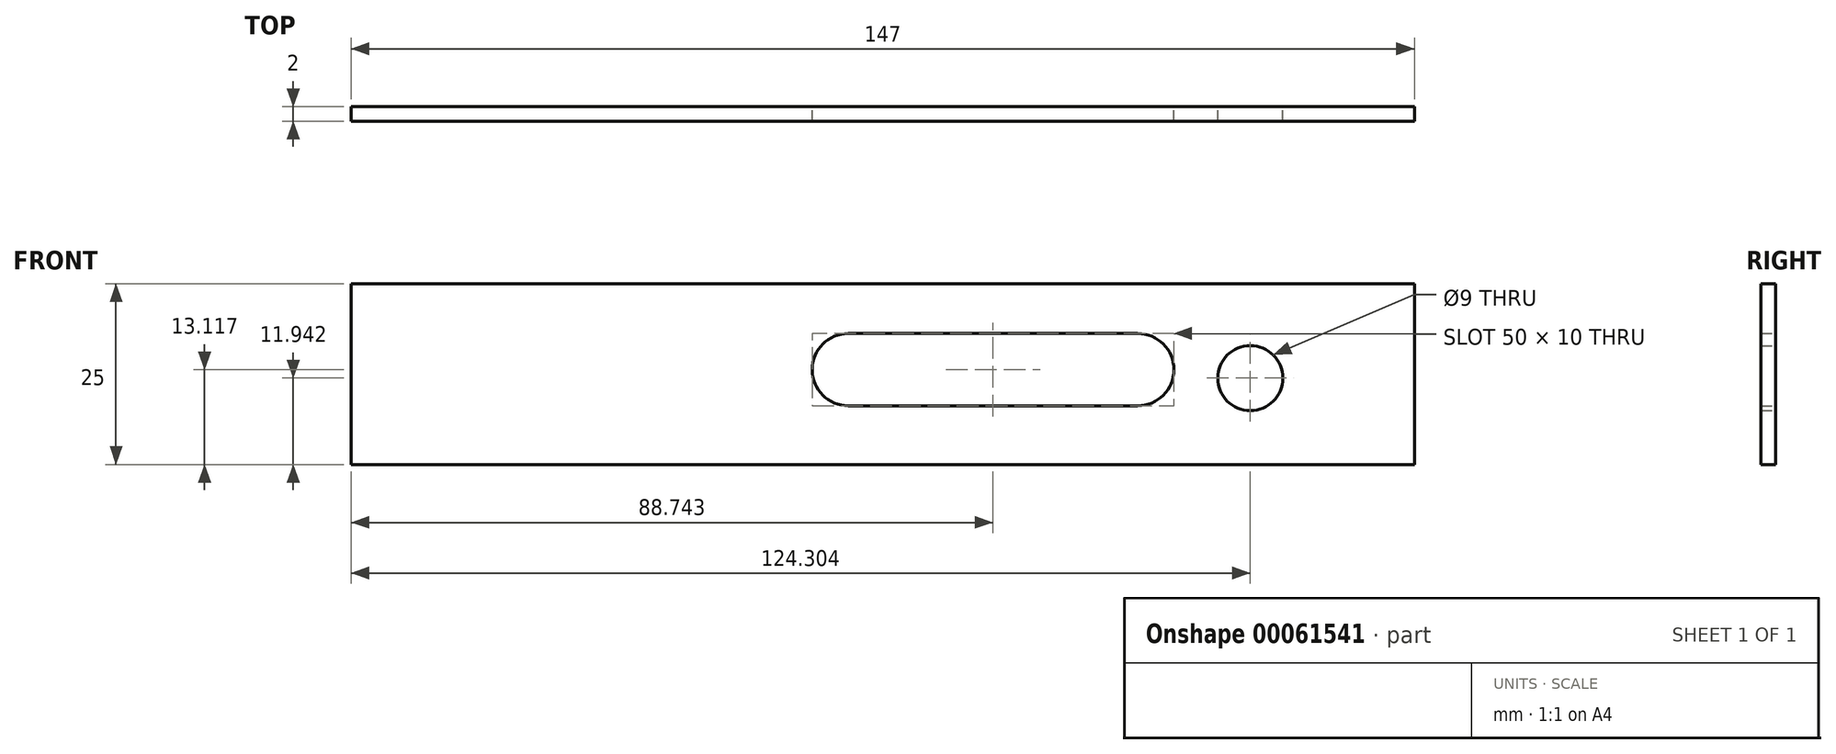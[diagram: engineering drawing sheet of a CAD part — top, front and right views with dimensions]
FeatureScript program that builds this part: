
annotation { "Feature Type Name" : "Feature", "Feature Type Description" : "" }
export const myFeature = defineFeature(function(context is Context, id is Id, definition is map)
    precondition{}
    {
        {
            var Q0;
            Q0=qCreatedBy(makeId("Front.planeOp"),FACE);
            var sketch = newSketch(context, id + "F0", { "sketchPlane" : qUnion([Q0])});
            skLineSegment(sketch, "E0.bottom", {"start": v(-75.22, 9.59) * mm, "end": v(71.78, 9.59) * mm});
            skLineSegment(sketch, "E0.top", {"start": v(-75.22, -15.41) * mm, "end": v(71.78, -15.41) * mm});
            skLineSegment(sketch, "E0.left", {"start": v(-75.22, 9.59) * mm, "end": v(-75.22, -15.41) * mm});
            skLineSegment(sketch, "E0.right", {"start": v(71.78, 9.59) * mm, "end": v(71.78, -15.41) * mm});
            skCircle(sketch, "E1", {"center": v(49.08, -3.47) * mm, "radius": 4.5 * mm});
            skLineSegment(sketch, "E2.bottom", {"start": v(-6.48, 2.7) * mm, "end": v(33.52, 2.7) * mm});
            skLineSegment(sketch, "E2.top", {"start": v(-6.48, -7.3) * mm, "end": v(33.52, -7.3) * mm});
            skLineSegment(sketch, "E2.left", {"start": v(-11.48, -2.3) * mm, "end": v(-11.48, -2.3) * mm});
            skLineSegment(sketch, "E2.right", {"start": v(38.52, -2.3) * mm, "end": v(38.52, -2.3) * mm});
            skPoint(sketch, "E3.visualSharp", {"position": v(-11.48, 2.7) * mm});
            skArc(sketch, "E3.filletArc", {"start": v(-6.48, 2.7) * mm, "mid": v(-10.01, 1.24) * mm, "end": v(-11.48, -2.3) * mm});
            skPoint(sketch, "E4.visualSharp", {"position": v(-11.48, -7.3) * mm});
            skArc(sketch, "E4.filletArc", {"start": v(-11.48, -2.3) * mm, "mid": v(-10.01, -5.83) * mm, "end": v(-6.48, -7.3) * mm});
            skPoint(sketch, "E5.visualSharp", {"position": v(38.52, -7.3) * mm});
            skArc(sketch, "E5.filletArc", {"start": v(33.52, -7.3) * mm, "mid": v(37.06, -5.83) * mm, "end": v(38.52, -2.3) * mm});
            skPoint(sketch, "E6.visualSharp", {"position": v(38.52, 2.7) * mm});
            skArc(sketch, "E6.filletArc", {"start": v(38.52, -2.3) * mm, "mid": v(37.06, 1.24) * mm, "end": v(33.52, 2.7) * mm});
            skSolve(sketch);
        }
        {
            var Q0;
            Q0=makeQuery(id+"F0.imprint","IMPRINT",FACE,{"disambiguationData":[TD([[makeQuery(id+"F0.imprint","IMPRINT",EDGE,{"derivedFrom":sQuery(id+"F0.wireOp",EDGE,"E0.bottom")}),-1.0]])]});
            extrude(context, id + "F1", {"entities" : qUnion([Q0]), "depth" : 2 * mm});
        }
    });
